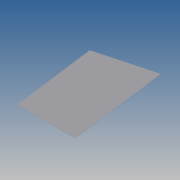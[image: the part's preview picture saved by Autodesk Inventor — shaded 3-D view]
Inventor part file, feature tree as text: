
AUTODESK INVENTOR PART (.ipt)
format: ipt  version: 2014 SP1 (Build 180222100, 222)  size: 73,728 bytes
history: native  units: in
note: dims shown in document units (in); Inventor stores cm internally (conversion verified against a paired STEP export)
features: extrude x1, sketch x1
ambient origin geometry x8: Origin, YZ Plane, XZ Plane, XY Plane, X Axis, Y Axis, Z Axis, Center Point
bodies: Solid1 (feature_tree)
feature tree (2):
  extrude  "Extrusion1"  Depth=0.0394in
  sketch  "Sketch1"  dims[d0=314.9606in d1=314.9606in d2=165.0deg d3=251.5748in d4=1.1853in d7=1.9685in d8=1.9685in d9=0.0394in d10=0.0in]
